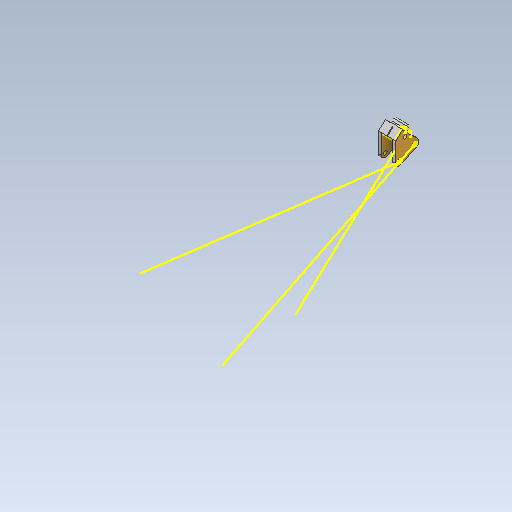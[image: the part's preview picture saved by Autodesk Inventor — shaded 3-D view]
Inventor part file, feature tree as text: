
AUTODESK INVENTOR PART (.ipt)
format: ipt  version: 2020 (Build 240168000, 168)  size: 312,832 bytes
history: native  units: mm
features: sketch x7, other x4, projected_geometry x3, extrude x2
ambient origin geometry x8: Origin, YZ Plane, XZ Plane, XY Plane, X Axis, Y Axis, Z Axis, Center Point
bodies: Solid1 (feature_tree)
feature tree (16):
  other  "preadator nano fixed mount template.iam"
  other  "Kauri modular camera mount HDzero micro v1 mirror.ipt:1"
  other  "Kauri modular camera mount HDzero micro v1.ipt:1"
  other  "camera housing V1.ipt:1"
  extrude  "Extrusion1"  Depth=10.0mm TaperAngle=0.0deg
  extrude  "Extrusion2"  [1 undecoded]
  sketch  "Sketch1"  dims[d0=10.0mm d1=10.0mm d2=0.0mm]
  sketch  "Sketch1_1"  dims[d3=10.0mm d4=0.0mm]
  sketch  "Sketch6"
  sketch  "Sketch10"
  sketch  "Sketch11"
  sketch  "Sketch7"
  projected_geometry  "Projected Loop1"
  sketch  "Sketch8"
  projected_geometry  "Projected Loop2"
  projected_geometry  "Projected Loop3"
note: 1 required parameter value undecoded (feature->parameter linkage not recoverable at this tier; creation-order binding heuristic only, values carry confidence <= 0.55)
